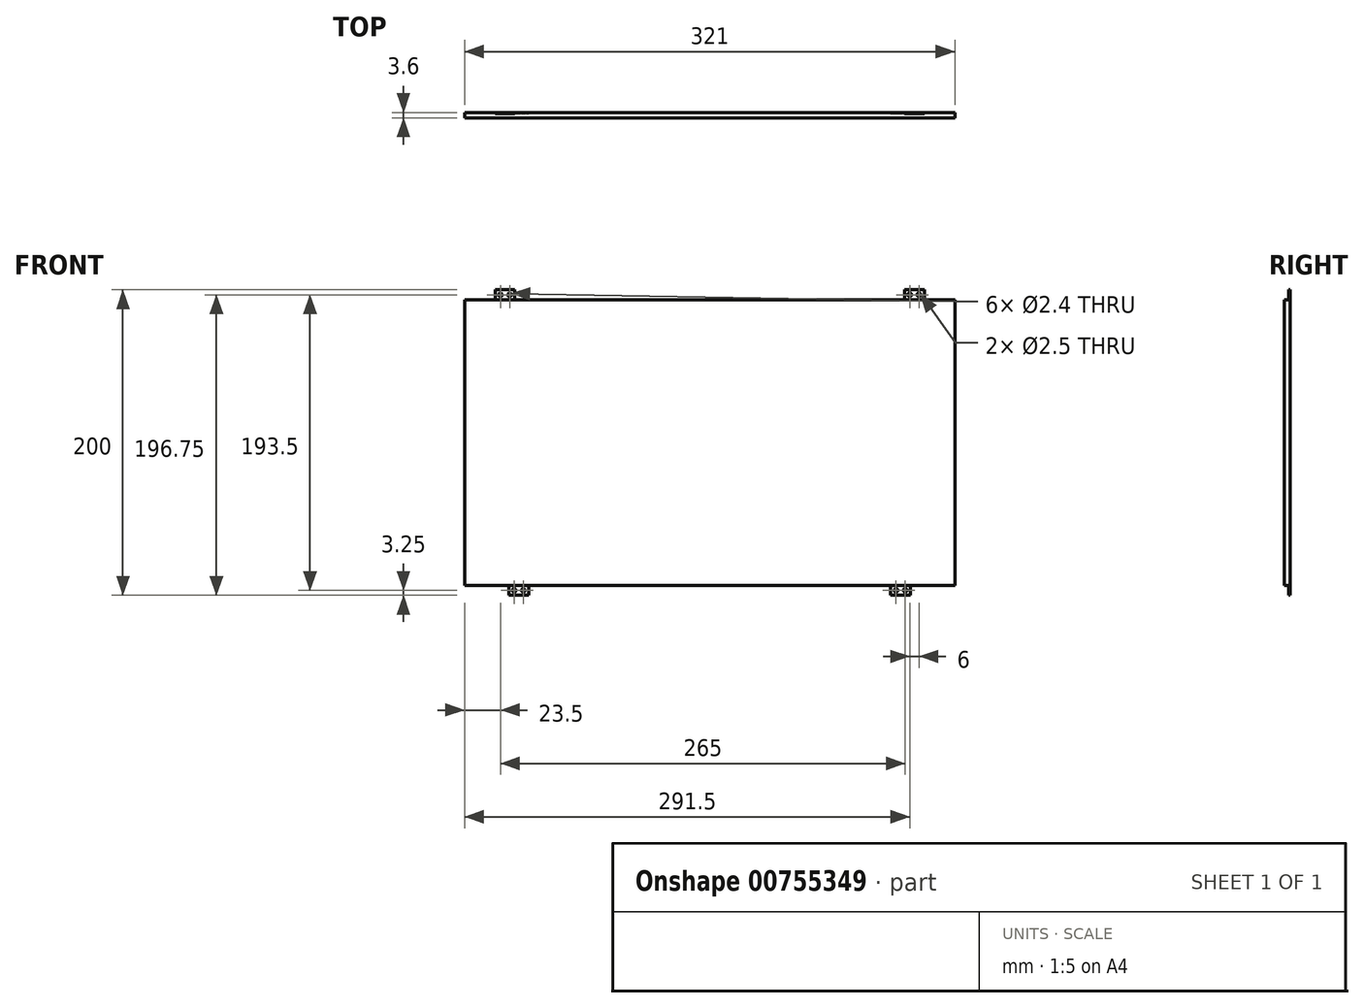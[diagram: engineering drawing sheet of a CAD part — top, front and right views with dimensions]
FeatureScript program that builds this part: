
annotation { "Feature Type Name" : "Feature", "Feature Type Description" : "" }
export const myFeature = defineFeature(function(context is Context, id is Id, definition is map)
    precondition{}
    {
        {
            var Q0;
            Q0=qCreatedBy(makeId("Front.planeOp"),FACE);
            var sketch = newSketch(context, id + "F0", { "sketchPlane" : qUnion([Q0])});
            skLineSegment(sketch, "E0.bottom", {"start": v(0, 0) * mm, "end": v(321, 0) * mm});
            skLineSegment(sketch, "E0.top", {"start": v(0, 187) * mm, "end": v(321, 187) * mm});
            skLineSegment(sketch, "E0.left", {"start": v(0, 0) * mm, "end": v(0, 187) * mm});
            skLineSegment(sketch, "E0.right", {"start": v(321, 0) * mm, "end": v(321, 187) * mm});
            skLineSegment(sketch, "E1.bottom", {"start": v(20, 187) * mm, "end": v(33, 187) * mm});
            skLineSegment(sketch, "E1.top", {"start": v(20, 193.5) * mm, "end": v(33, 193.5) * mm});
            skLineSegment(sketch, "E1.left", {"start": v(20, 187) * mm, "end": v(20, 193.5) * mm});
            skLineSegment(sketch, "E1.right", {"start": v(33, 187) * mm, "end": v(33, 193.5) * mm});
            skLineSegment(sketch, "E2.bottom", {"start": v(288, 187) * mm, "end": v(301, 187) * mm});
            skLineSegment(sketch, "E2.top", {"start": v(288, 193.5) * mm, "end": v(301, 193.5) * mm});
            skLineSegment(sketch, "E2.left", {"start": v(288, 187) * mm, "end": v(288, 193.5) * mm});
            skLineSegment(sketch, "E2.right", {"start": v(301, 187) * mm, "end": v(301, 193.5) * mm});
            skLineSegment(sketch, "E3.bottom", {"start": v(29, 0) * mm, "end": v(42, 0) * mm});
            skLineSegment(sketch, "E3.top", {"start": v(29, -6.5) * mm, "end": v(42, -6.5) * mm});
            skLineSegment(sketch, "E3.left", {"start": v(29, 0) * mm, "end": v(29, -6.5) * mm});
            skLineSegment(sketch, "E3.right", {"start": v(42, 0) * mm, "end": v(42, -6.5) * mm});
            skLineSegment(sketch, "E4.bottom", {"start": v(279, 0) * mm, "end": v(292, 0) * mm});
            skLineSegment(sketch, "E4.top", {"start": v(279, -6.5) * mm, "end": v(292, -6.5) * mm});
            skLineSegment(sketch, "E4.left", {"start": v(279, 0) * mm, "end": v(279, -6.5) * mm});
            skLineSegment(sketch, "E4.right", {"start": v(292, 0) * mm, "end": v(292, -6.5) * mm});
            skCircle(sketch, "E5", {"center": v(23.5, 190.25) * mm, "radius": 1.2 * mm});
            skPoint(sketch, "E5.centerSnap0", {"position": v(33, 190.25) * mm});
            skCircle(sketch, "E6", {"center": v(29.5, 190.25) * mm, "radius": 1.2 * mm});
            skCircle(sketch, "E7", {"center": v(32.5, -3.25) * mm, "radius": 1.2 * mm});
            skPoint(sketch, "E7.centerSnap0", {"position": v(29, -3.25) * mm});
            skCircle(sketch, "E8", {"center": v(38.5, -3.25) * mm, "radius": 1.2 * mm});
            skPoint(sketch, "E8.centerSnap0", {"position": v(42, -3.25) * mm});
            skCircle(sketch, "E9", {"center": v(288.5, -3.25) * mm, "radius": 1.2 * mm});
            skPoint(sketch, "E9.centerSnap0", {"position": v(292, -3.25) * mm});
            skCircle(sketch, "E10", {"center": v(282.5, -3.25) * mm, "radius": 1.2 * mm});
            skPoint(sketch, "E10.centerSnap0", {"position": v(279, -3.25) * mm});
            skCircle(sketch, "E11", {"center": v(291.5, 190.25) * mm, "radius": 1.25 * mm});
            skPoint(sketch, "E11.centerSnap0", {"position": v(288, 190.25) * mm});
            skCircle(sketch, "E12", {"center": v(297.5, 190.25) * mm, "radius": 1.25 * mm});
            skPoint(sketch, "E12.centerSnap0", {"position": v(301, 190.25) * mm});
            skSolve(sketch);
        }
        {
            var Q0;
            Q0 = qSketchRegion(id + "F0", true);
            extrude(context, id + "F1", {"entities" : qUnion([Q0]), "depth" : .8 * mm, "offsetDistance" : 25 * mm});
        }
        {
            var Q0;
            Q0=makeQuery(id+"F1.opExtrude","CAP_FACE",FACE,{"disambiguationData":[OSD([sQuery(id+"F0.wireOp",EDGE,"E0.bottom"),sQuery(id+"F0.wireOp",EDGE,"E0.top"),sQuery(id+"F0.wireOp",EDGE,"E0.left"),sQuery(id+"F0.wireOp",EDGE,"E0.right"),sQuery(id+"F0.wireOp",EDGE,"E1.top"),sQuery(id+"F0.wireOp",EDGE,"E1.left"),sQuery(id+"F0.wireOp",EDGE,"E1.right"),sQuery(id+"F0.wireOp",EDGE,"E2.top"),sQuery(id+"F0.wireOp",EDGE,"E2.left"),sQuery(id+"F0.wireOp",EDGE,"E2.right"),sQuery(id+"F0.wireOp",EDGE,"E3.top"),sQuery(id+"F0.wireOp",EDGE,"E3.left"),sQuery(id+"F0.wireOp",EDGE,"E3.right"),sQuery(id+"F0.wireOp",EDGE,"E4.top"),sQuery(id+"F0.wireOp",EDGE,"E4.left"),sQuery(id+"F0.wireOp",EDGE,"E4.right"),sQuery(id+"F0.wireOp",EDGE,"E5"),sQuery(id+"F0.wireOp",EDGE,"E6"),sQuery(id+"F0.wireOp",EDGE,"E7"),sQuery(id+"F0.wireOp",EDGE,"E8"),sQuery(id+"F0.wireOp",EDGE,"E9"),sQuery(id+"F0.wireOp",EDGE,"E10"),sQuery(id+"F0.wireOp",EDGE,"E11"),sQuery(id+"F0.wireOp",EDGE,"E12")])],"isStart":false});
            var sketch = newSketch(context, id + "F2", { "sketchPlane" : qUnion([Q0])});
            skLineSegment(sketch, "E13.bottom", {"start": v(0, 187) * mm, "end": v(321, 187) * mm});
            skLineSegment(sketch, "E13.top", {"start": v(0, 0) * mm, "end": v(321, 0) * mm});
            skLineSegment(sketch, "E13.left", {"start": v(0, 187) * mm, "end": v(0, 0) * mm});
            skLineSegment(sketch, "E13.right", {"start": v(321, 187) * mm, "end": v(321, 0) * mm});
            skSolve(sketch);
        }
        {
            var Q0;
            Q0 = qSketchRegion(id + "F2", true);
            extrude(context, id + "F3", {"entities" : qUnion([Q0]), "operationType" : NewBodyOperationType.ADD, "depth" : 2.8 * mm, "offsetDistance" : 25 * mm});
        }
    });
